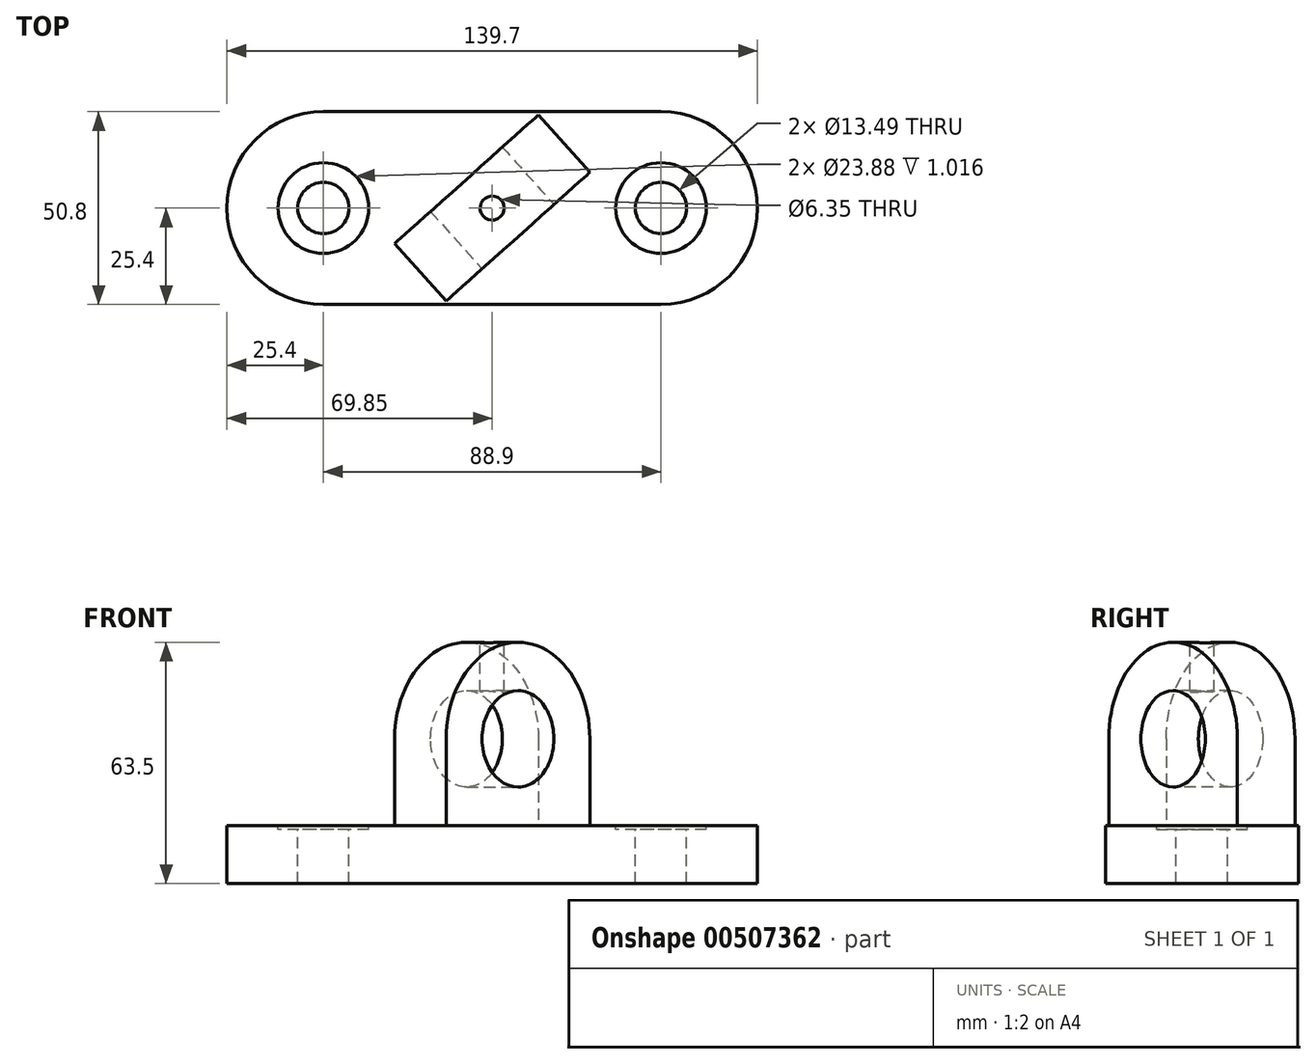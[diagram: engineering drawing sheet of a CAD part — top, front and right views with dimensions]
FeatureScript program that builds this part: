
annotation { "Feature Type Name" : "Feature", "Feature Type Description" : "" }
export const myFeature = defineFeature(function(context is Context, id is Id, definition is map)
    precondition{}
    {
        {
            var Q0;
            Q0=qCreatedBy(makeId("Top.planeOp"),FACE);
            var sketch = newSketch(context, id + "F0", { "sketchPlane" : qUnion([Q0])});
            skLineSegment(sketch, "E0", {"start": v(-44.45, 25.4) * mm, "end": v(44.45, 25.4) * mm});
            skLineSegment(sketch, "E1", {"start": v(-44.45, -25.4) * mm, "end": v(44.45, -25.4) * mm});
            skArc(sketch, "E2", {"start": v(-44.45, 25.4) * mm, "mid": v(-69.85, 0) * mm, "end": v(-44.45, -25.4) * mm});
            skArc(sketch, "E3", {"start": v(44.45, -25.4) * mm, "mid": v(69.85, 0) * mm, "end": v(44.45, 25.4) * mm});
            skCircle(sketch, "E4", {"center": v(44.45, 0) * mm, "radius": 11.94 * mm});
            skCircle(sketch, "E5", {"center": v(44.45, 0) * mm, "radius": 6.74 * mm});
            skPoint(sketch, "E6", {"position": v(0, 25.4) * mm});
            skCircle(sketch, "E7", {"center": v(-44.45, 0) * mm, "radius": 6.74 * mm});
            skCircle(sketch, "E8", {"center": v(-44.45, 0) * mm, "radius": 11.94 * mm});
            skLineSegment(sketch, "E9", {"start": v(-25.7, -9.38) * mm, "end": v(12.14, 24.51) * mm});
            skLineSegment(sketch, "E10", {"start": v(-12.14, -24.51) * mm, "end": v(25.7, 9.38) * mm});
            skLineSegment(sketch, "E11", {"start": v(-25.7, -9.38) * mm, "end": v(-12.14, -24.51) * mm});
            skLineSegment(sketch, "E12", {"start": v(12.14, 24.51) * mm, "end": v(25.7, 9.38) * mm});
            skSolve(sketch);
        }
        {
            var Q0;
            {var subQ0=sQuery(id+"F0.wireOp",EDGE,"E2");Q0=makeQuery(id+"F0.imprint","IMPRINT",FACE,{"disambiguationData":[TD([[makeQuery(id+"F0.imprint","IMPRINT",EDGE,{"derivedFrom":subQ0}),1.0]])]});}
            var Q1;
            {var subQ0=sQuery(id+"F0.wireOp",EDGE,"E3");Q1=makeQuery(id+"F0.imprint","IMPRINT",FACE,{"disambiguationData":[TD([[makeQuery(id+"F0.imprint","IMPRINT",EDGE,{"derivedFrom":subQ0}),1.0]])]});}
            var Q2;
            Q2=makeQuery(id+"F0.imprint","IMPRINT",FACE,{"disambiguationData":[TD([[makeQuery(id+"F0.imprint","IMPRINT",EDGE,{"derivedFrom":sQuery(id+"F0.wireOp",EDGE,"0pdgy7kQ-NDVB-uREp-v4q6-HqcUGQRuLzJY")}),1.0]])]});
            var Q3;
            Q3=makeQuery(id+"F0.imprint","IMPRINT",FACE,{"disambiguationData":[TD([[makeQuery(id+"F0.imprint","IMPRINT",EDGE,{"derivedFrom":sQuery(id+"F0.wireOp",EDGE,"E7")}),-1.0]])]});
            var Q4;
            Q4=makeQuery(id+"F0.imprint","IMPRINT",FACE,{"disambiguationData":[TD([[makeQuery(id+"F0.imprint","IMPRINT",EDGE,{"derivedFrom":sQuery(id+"F0.wireOp",EDGE,"E4")}),1.0]])]});
            var Q5;
            Q5=makeQuery(id+"F0.imprint","IMPRINT",FACE,{"disambiguationData":[TD([[makeQuery(id+"F0.imprint","IMPRINT",EDGE,{"derivedFrom":sQuery(id+"F0.wireOp",EDGE,"E9")}),-1.0]])]});
            extrude(context, id + "F1", {"entities" : qUnion([Q0, Q1, Q2, Q3, Q4, Q5]), "oppositeDirection" : true, "depth" : 15.24 * mm});
        }
        {
            var Q0;
            Q0=makeQuery(id+"F0.imprint","IMPRINT",FACE,{"disambiguationData":[TD([[makeQuery(id+"F0.imprint","IMPRINT",EDGE,{"derivedFrom":sQuery(id+"F0.wireOp",EDGE,"E7")}),-1.0]])]});
            var Q1;
            Q1=makeQuery(id+"F0.imprint","IMPRINT",FACE,{"disambiguationData":[TD([[makeQuery(id+"F0.imprint","IMPRINT",EDGE,{"derivedFrom":sQuery(id+"F0.wireOp",EDGE,"E4")}),1.0]])]});
            extrude(context, id + "F2", {"entities" : qUnion([Q0, Q1]), "operationType" : NewBodyOperationType.REMOVE, "oppositeDirection" : true, "depth" : 1.02 * mm});
        }
        {
            var Q0;
            {var subQ0=sQuery(id+"F0.wireOp",EDGE,"E3");Q0=makeQuery(id+"F0.imprint","IMPRINT",FACE,{"disambiguationData":[TD([[makeQuery(id+"F0.imprint","IMPRINT",EDGE,{"derivedFrom":subQ0}),1.0]])]});}
            cPlane(context, id + "F3", {"entities" : qUnion([Q0]), "cplaneType" : CPlaneType.OFFSET, "offset" : 48.26 * mm, "width" : 152.4 * mm, "height" : 152.4 * mm});
        }
        {
            var Q0;
            Q0=makeQuery(id+"F0.imprint","IMPRINT",FACE,{"disambiguationData":[TD([[makeQuery(id+"F0.imprint","IMPRINT",EDGE,{"derivedFrom":sQuery(id+"F0.wireOp",EDGE,"E9")}),-1.0]])]});
            extrude(context, id + "F4", {"entities" : qUnion([Q0]), "operationType" : NewBodyOperationType.ADD, "depth" : 48.26 * mm});
        }
        {
            var Q0;
            Q0=makeQuery(id+"F4.opExtrude","CAP_EDGE",EDGE,{"disambiguationData":[OSD([sQuery(id+"F0.wireOp",EDGE,"E11")])],"isStart":false});
            var Q1;
            Q1=makeQuery(id+"F4.opExtrude","CAP_EDGE",EDGE,{"disambiguationData":[OSD([sQuery(id+"F0.wireOp",EDGE,"E12")])],"isStart":false});
            fillet(context, id + "F5", {"entities" : qUnion([Q0, Q1]), "radius" : 25.4 * mm, "tangentPropagation" : true, "allowEdgeOverflow" : false});
        }
        {
            var Q0;
            Q0=makeQuery(id+"F4.opExtrude","SWEPT_FACE",FACE,{"disambiguationData":[OSD([sQuery(id+"F0.wireOp",EDGE,"E10")])]});
            var sketch = newSketch(context, id + "F6", { "sketchPlane" : qUnion([Q0])});
            skPoint(sketch, "E13", {"position": v(0, 22.86) * mm});
            skCircle(sketch, "E14", {"center": v(0, 22.86) * mm, "radius": 12.7 * mm});
            skSolve(sketch);
        }
        {
            var Q0;
            Q0=makeQuery(id+"F6.imprint","IMPRINT",FACE,{"disambiguationData":[TD([[makeQuery(id+"F6.imprint","IMPRINT",EDGE,{"derivedFrom":sQuery(id+"F6.wireOp",EDGE,"E14")}),1.0]])]});
            extrude(context, id + "F7", {"entities" : qUnion([Q0]), "operationType" : NewBodyOperationType.REMOVE, "oppositeDirection" : true, "depth" : 25.4 * mm});
        }
        {
            var Q0;
            Q0=qCreatedBy(id+"F3.planeOp",FACE);
            var sketch = newSketch(context, id + "F8", { "sketchPlane" : qUnion([Q0])});
            skCircle(sketch, "E15", {"center": v(0, 0) * mm, "radius": 3.17 * mm});
            skSolve(sketch);
        }
        {
            var Q0;
            Q0=makeQuery(id+"F8.imprint","IMPRINT",FACE,{"disambiguationData":[TD([[makeQuery(id+"F8.imprint","IMPRINT",EDGE,{"derivedFrom":sQuery(id+"F8.wireOp",EDGE,"E15")}),1.0]])]});
            extrude(context, id + "F9", {"entities" : qUnion([Q0]), "operationType" : NewBodyOperationType.REMOVE, "endBound" : BoundingType.UP_TO_NEXT, "oppositeDirection" : true, "depth" : 25.4 * mm});
        }
    });
